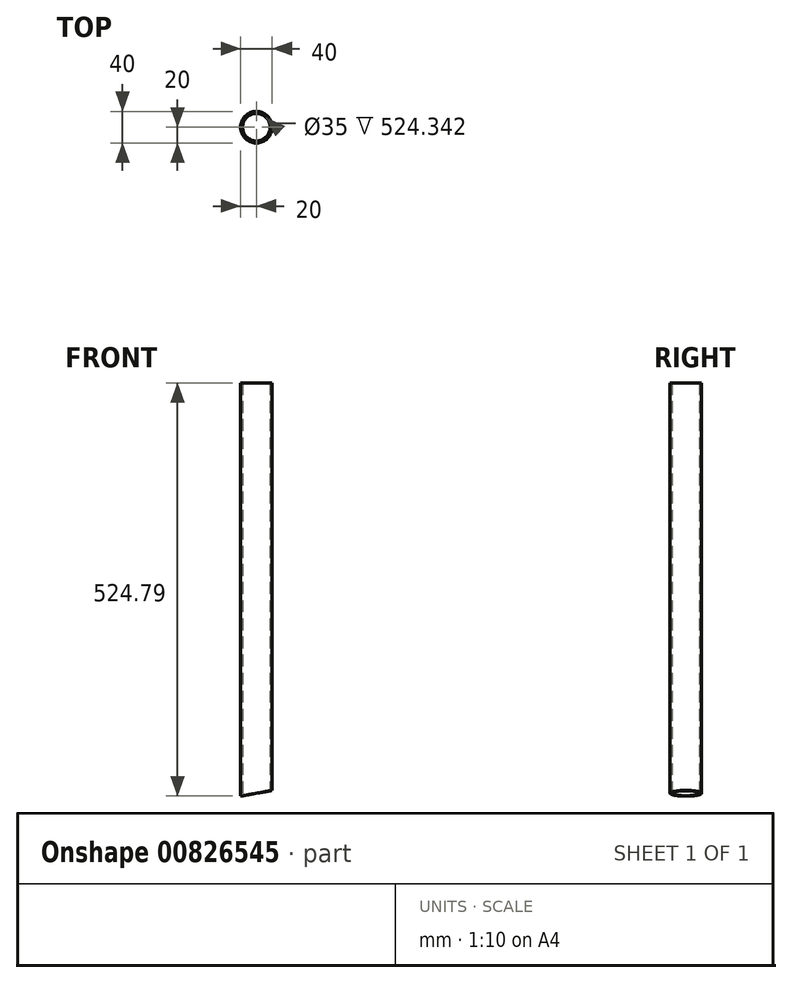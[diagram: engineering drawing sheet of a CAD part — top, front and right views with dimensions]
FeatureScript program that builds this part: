
annotation { "Feature Type Name" : "Feature", "Feature Type Description" : "" }
export const myFeature = defineFeature(function(context is Context, id is Id, definition is map)
    precondition{}
    {
        {
            var Q0;
            Q0=qCreatedBy(makeId("Top.planeOp"),FACE);
            var sketch = newSketch(context, id + "F0", { "sketchPlane" : qUnion([Q0])});
            skCircle(sketch, "E0", {"center": v(0, 0) * mm, "radius": 20 * mm});
            skCircle(sketch, "E1", {"center": v(0, 0) * mm, "radius": 17.5 * mm});
            skSolve(sketch);
        }
        {
            var Q0;
            Q0=makeQuery(id+"F0.imprint","IMPRINT",FACE,{"disambiguationData":[TD([[makeQuery(id+"F0.imprint","IMPRINT",EDGE,{"derivedFrom":sQuery(id+"F0.wireOp",EDGE,"E0")}),1.0]])]});
            extrude(context, id + "F1", {"entities" : qUnion([Q0]), "depth" : ((866 - 342) + 0.79) * mm, "offsetDistance" : 25 * mm});
        }
        {
            var Q0;
            Q0=qCreatedBy(makeId("Front.planeOp"),FACE);
            var sketch = newSketch(context, id + "F2", { "sketchPlane" : qUnion([Q0])});
            skLineSegment(sketch, "E2", {"start": v(-20, 0) * mm, "end": v(0, 0) * mm});
            skLineSegment(sketch, "E3", {"start": v(0, 0) * mm, "end": v(20, 0) * mm});
            skLineSegment(sketch, "E4", {"start": v(20, 0) * mm, "end": v(20, 19.08) * mm});
            skLineSegment(sketch, "E5", {"start": v(-20, 0) * mm, "end": v(20, 7.2) * mm});
            skSolve(sketch);
        }
        {
            var Q0;
            Q0=qSketchRegion(id+"F2",true);
            extrude(context, id + "F3", {"entities" : qUnion([Q0]), "operationType" : NewBodyOperationType.REMOVE, "endBound" : BoundingType.SYMMETRIC, "oppositeDirection" : true, "depth" : 50 * mm, "offsetDistance" : 25 * mm});
        }
    });
